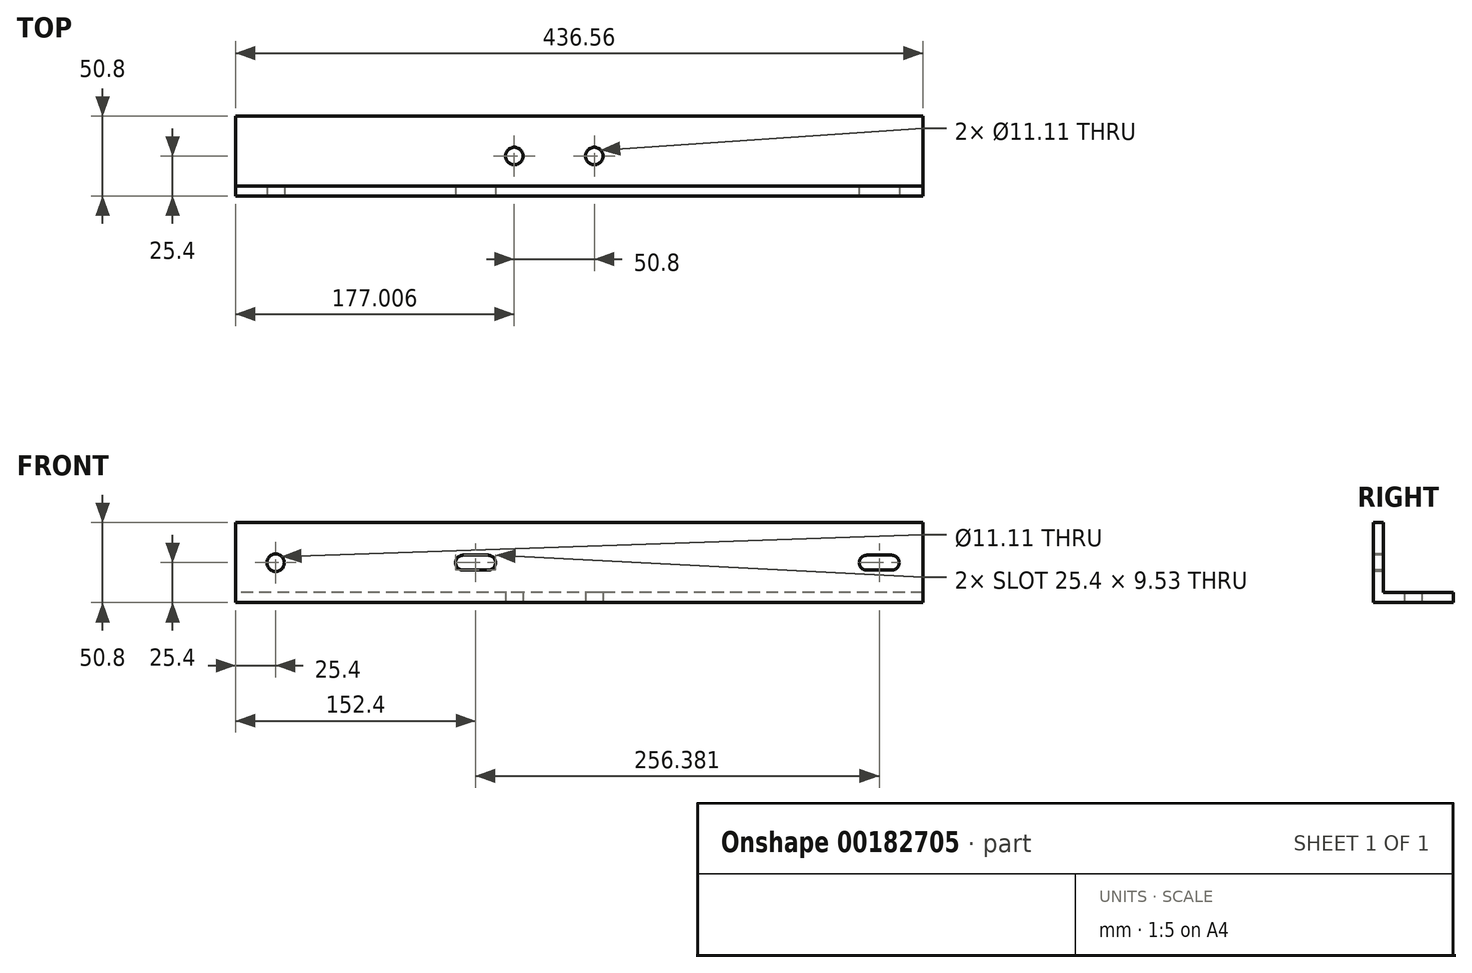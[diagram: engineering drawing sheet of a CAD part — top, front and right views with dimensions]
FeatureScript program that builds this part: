
annotation { "Feature Type Name" : "Feature", "Feature Type Description" : "" }
export const myFeature = defineFeature(function(context is Context, id is Id, definition is map)
    precondition{}
    {
        {
            var Q0;
            Q0=qCreatedBy(makeId("Right.planeOp"),FACE);
            var sketch = newSketch(context, id + "F0", { "sketchPlane" : qUnion([Q0])});
            skLineSegment(sketch, "E0", {"start": v(0, 0) * mm, "end": v(0, 50.8) * mm});
            skLineSegment(sketch, "E1", {"start": v(0, 50.8) * mm, "end": v(6.35, 50.8) * mm});
            skLineSegment(sketch, "E2", {"start": v(6.35, 50.8) * mm, "end": v(6.35, 6.35) * mm});
            skLineSegment(sketch, "E3", {"start": v(6.35, 6.35) * mm, "end": v(50.8, 6.35) * mm});
            skLineSegment(sketch, "E4", {"start": v(50.8, 6.35) * mm, "end": v(50.8, 0) * mm});
            skLineSegment(sketch, "E5", {"start": v(50.8, 0) * mm, "end": v(0, 0) * mm});
            skSolve(sketch);
        }
        {
            var Q0;
            Q0=makeQuery(id+"F0.imprint","IMPRINT",FACE,{"disambiguationData":[TD([[makeQuery(id+"F0.imprint","IMPRINT",EDGE,{"derivedFrom":sQuery(id+"F0.wireOp",EDGE,"E0")}),-1.0]])]});
            extrude(context, id + "F1", {"entities" : qUnion([Q0]), "depth" : 436.56 * mm});
        }
        {
            var Q0;
            Q0=makeQuery(id+"F1.opExtrude","SWEPT_FACE",FACE,{"disambiguationData":[OSD([sQuery(id+"F0.wireOp",EDGE,"E0")])]});
            var sketch = newSketch(context, id + "F2", { "sketchPlane" : qUnion([Q0])});
            skCircle(sketch, "E6", {"center": v(25.4, 25.4) * mm, "radius": 5.56 * mm});
            skLineSegment(sketch, "E7", {"start": v(144.46, 25.4) * mm, "end": v(160.34, 25.4) * mm});
            skArc(sketch, "E8.0.startCap", {"start": v(144.46, 20.64) * mm, "mid": v(139.7, 25.4) * mm, "end": v(144.46, 30.16) * mm});
            skArc(sketch, "E8.0.endCap", {"start": v(160.34, 30.16) * mm, "mid": v(165.1, 25.4) * mm, "end": v(160.34, 20.64) * mm});
            skLineSegment(sketch, "E8.0.left", {"start": v(144.46, 30.16) * mm, "end": v(160.34, 30.16) * mm});
            skLineSegment(sketch, "E8.0.right", {"start": v(144.46, 20.64) * mm, "end": v(160.34, 20.64) * mm});
            skLineSegment(sketch, "E9", {"start": v(400.84, 25.4) * mm, "end": v(416.72, 25.4) * mm});
            skArc(sketch, "E10.0.startCap", {"start": v(400.84, 20.64) * mm, "mid": v(396.08, 25.4) * mm, "end": v(400.84, 30.16) * mm});
            skArc(sketch, "E10.0.endCap", {"start": v(416.72, 30.16) * mm, "mid": v(421.48, 25.4) * mm, "end": v(416.72, 20.64) * mm});
            skLineSegment(sketch, "E10.0.left", {"start": v(400.84, 30.16) * mm, "end": v(416.72, 30.16) * mm});
            skLineSegment(sketch, "E10.0.right", {"start": v(400.84, 20.64) * mm, "end": v(416.72, 20.64) * mm});
            skSolve(sketch);
        }
        {
            var Q0;
            Q0 = qSketchRegion(id + "F2", true);
            extrude(context, id + "F3", {"entities" : qUnion([Q0]), "operationType" : NewBodyOperationType.REMOVE, "endBound" : BoundingType.THROUGH_ALL, "oppositeDirection" : true, "depth" : 25.4 * mm});
        }
        {
            var Q0;
            Q0=makeQuery(id+"F1.opExtrude","SWEPT_FACE",FACE,{"disambiguationData":[OSD([sQuery(id+"F0.wireOp",EDGE,"E5")])]});
            var sketch = newSketch(context, id + "F4", { "sketchPlane" : qUnion([Q0])});
            skCircle(sketch, "E11", {"center": v(177, -25.4) * mm, "radius": 5.56 * mm});
            skCircle(sketch, "E12", {"center": v(227.8, -25.4) * mm, "radius": 5.56 * mm});
            skSolve(sketch);
        }
        {
            var Q0;
            Q0=makeQuery(id+"F4.imprint","IMPRINT",FACE,{"disambiguationData":[TD([[makeQuery(id+"F4.imprint","IMPRINT",EDGE,{"derivedFrom":sQuery(id+"F4.wireOp",EDGE,"E12")}),1.0]])]});
            var Q1;
            Q1=makeQuery(id+"F4.imprint","IMPRINT",FACE,{"disambiguationData":[TD([[makeQuery(id+"F4.imprint","IMPRINT",EDGE,{"derivedFrom":sQuery(id+"F4.wireOp",EDGE,"E11")}),1.0]])]});
            extrude(context, id + "F5", {"entities" : qUnion([Q0, Q1]), "operationType" : NewBodyOperationType.REMOVE, "endBound" : BoundingType.THROUGH_ALL, "oppositeDirection" : true, "depth" : 25.4 * mm});
        }
    });
